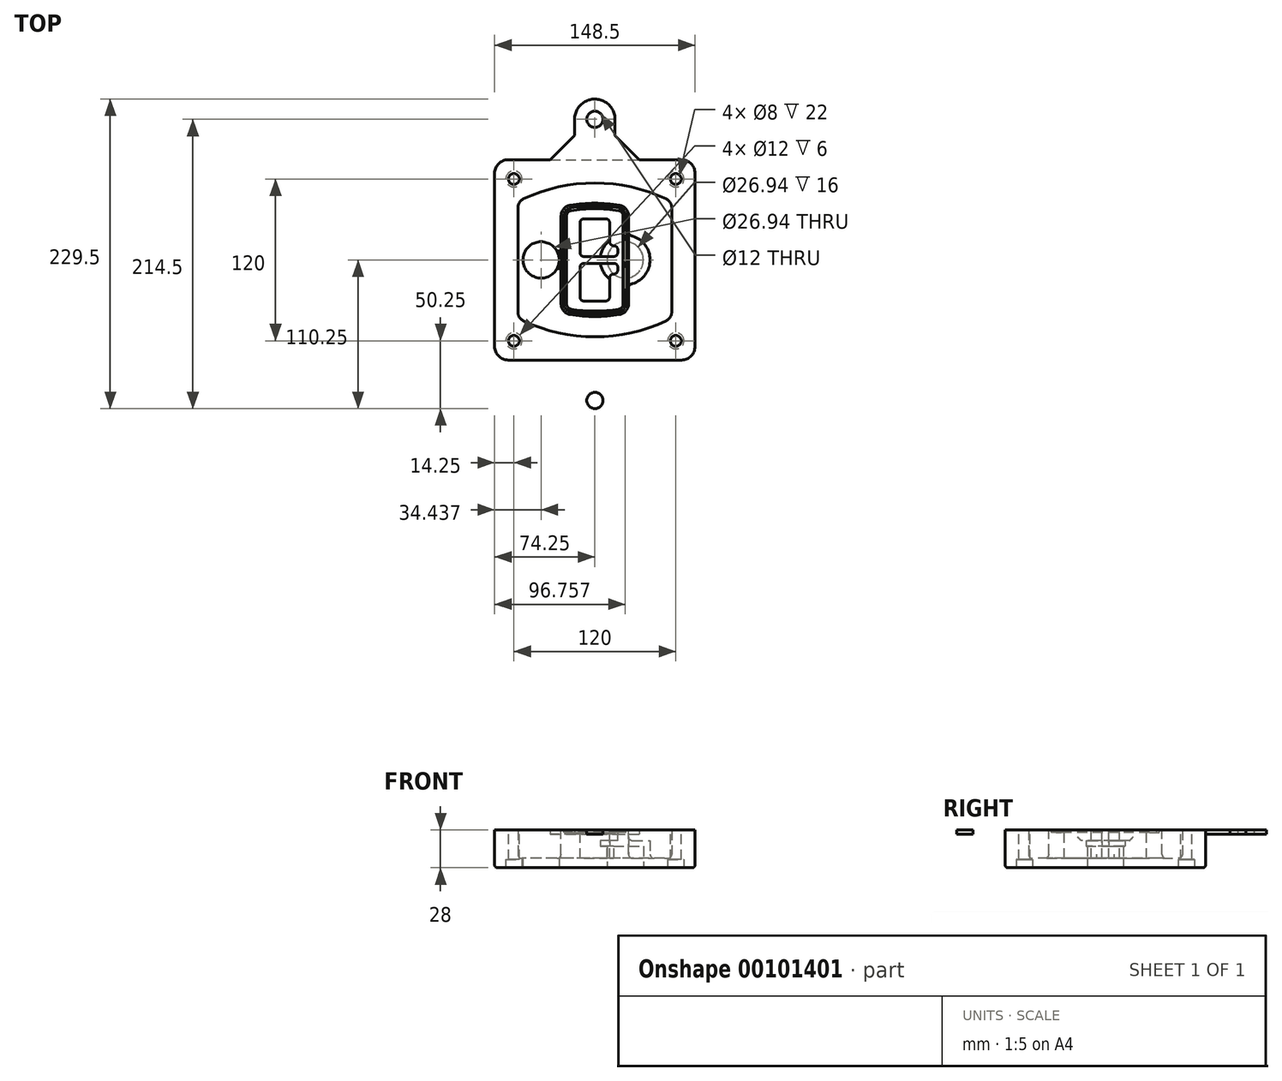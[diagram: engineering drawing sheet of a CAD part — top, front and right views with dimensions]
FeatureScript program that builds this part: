
annotation { "Feature Type Name" : "Feature", "Feature Type Description" : "" }
export const myFeature = defineFeature(function(context is Context, id is Id, definition is map)
    precondition{}
    {
        {
            var Q0;
            Q0=qCreatedBy(makeId("Top.planeOp"),FACE);
            var sketch = newSketch(context, id + "F0", { "sketchPlane" : qUnion([Q0])});
            skPoint(sketch, "E0.rect.middle", {"position": v(0, 0) * mm});
            skLineSegment(sketch, "E1.bottom", {"start": v(-64.25, -74.25) * mm, "end": v(64.25, -74.25) * mm});
            skLineSegment(sketch, "E1.top", {"start": v(-64.25, 74.25) * mm, "end": v(64.25, 74.25) * mm});
            skLineSegment(sketch, "E1.left", {"start": v(-74.25, -64.25) * mm, "end": v(-74.25, 64.25) * mm});
            skLineSegment(sketch, "E1.right", {"start": v(74.25, -64.25) * mm, "end": v(74.25, 64.25) * mm});
            skLineSegment(sketch, "E2", {"start": v(-74.25, 74.25) * mm, "end": v(74.25, -74.25) * mm, "construction": true});
            skLineSegment(sketch, "E3", {"start": v(74.25, 74.25) * mm, "end": v(-74.25, -74.25) * mm, "construction": true});
            skCircle(sketch, "E4", {"center": v(-60, 60) * mm, "radius": 4 * mm});
            skCircle(sketch, "E5", {"center": v(60, 60) * mm, "radius": 4 * mm});
            skCircle(sketch, "E6", {"center": v(60, -60) * mm, "radius": 4 * mm});
            skCircle(sketch, "E7", {"center": v(-60, -60) * mm, "radius": 4 * mm});
            skLineSegment(sketch, "E8", {"start": v(-60, 60) * mm, "end": v(60, 60) * mm, "construction": true});
            skLineSegment(sketch, "E9", {"start": v(60, 60) * mm, "end": v(60, -60) * mm, "construction": true});
            skLineSegment(sketch, "E10", {"start": v(60, -60) * mm, "end": v(-60, -60) * mm, "construction": true});
            skLineSegment(sketch, "E11", {"start": v(-60, -60) * mm, "end": v(-60, 60) * mm, "construction": true});
            skLineSegment(sketch, "E12", {"start": v(-60, 38.83) * mm, "end": v(-60, -38.83) * mm});
            skLineSegment(sketch, "E13", {"start": v(60, 38.83) * mm, "end": v(60, -38.83) * mm});
            skArc(sketch, "E14", {"start": v(54.26, 47.88) * mm, "mid": v(0, 60) * mm, "end": v(-54.26, 47.88) * mm});
            skArc(sketch, "E15", {"start": v(-54.26, -47.88) * mm, "mid": v(0, -60) * mm, "end": v(54.26, -47.88) * mm});
            skLineSegment(sketch, "E16", {"start": v(-60, 0) * mm, "end": v(60, 0) * mm, "construction": true});
            skPoint(sketch, "E17.visualSharp", {"position": v(-60, -45) * mm});
            skArc(sketch, "E17.filletArc", {"start": v(-60, -38.83) * mm, "mid": v(-58.44, -44.2) * mm, "end": v(-54.26, -47.88) * mm});
            skPoint(sketch, "E18.visualSharp", {"position": v(-60, 45) * mm});
            skArc(sketch, "E18.filletArc", {"start": v(-54.26, 47.88) * mm, "mid": v(-58.44, 44.2) * mm, "end": v(-60, 38.83) * mm});
            skPoint(sketch, "E19.visualSharp", {"position": v(60, 45) * mm});
            skArc(sketch, "E19.filletArc", {"start": v(60, 38.83) * mm, "mid": v(58.44, 44.2) * mm, "end": v(54.26, 47.88) * mm});
            skPoint(sketch, "E20.visualSharp", {"position": v(60, -45) * mm});
            skArc(sketch, "E20.filletArc", {"start": v(54.26, -47.88) * mm, "mid": v(58.44, -44.2) * mm, "end": v(60, -38.83) * mm});
            skPoint(sketch, "E21.visualSharp", {"position": v(-74.25, 74.25) * mm});
            skArc(sketch, "E21.filletArc", {"start": v(-64.25, 74.25) * mm, "mid": v(-71.32, 71.32) * mm, "end": v(-74.25, 64.25) * mm});
            skPoint(sketch, "E22.visualSharp", {"position": v(74.25, 74.25) * mm});
            skArc(sketch, "E22.filletArc", {"start": v(74.25, 64.25) * mm, "mid": v(71.32, 71.32) * mm, "end": v(64.25, 74.25) * mm});
            skPoint(sketch, "E23.visualSharp", {"position": v(74.25, -74.25) * mm});
            skArc(sketch, "E23.filletArc", {"start": v(64.25, -74.25) * mm, "mid": v(71.32, -71.32) * mm, "end": v(74.25, -64.25) * mm});
            skPoint(sketch, "E24.visualSharp", {"position": v(-74.25, -74.25) * mm});
            skArc(sketch, "E24.filletArc", {"start": v(-74.25, -64.25) * mm, "mid": v(-71.32, -71.32) * mm, "end": v(-64.25, -74.25) * mm});
            skArc(sketch, "E25.0", {"start": v(57, 38.83) * mm, "mid": v(55.9, 42.58) * mm, "end": v(52.98, 45.17) * mm});
            skLineSegment(sketch, "E25.1", {"start": v(57, 38.83) * mm, "end": v(57, -38.83) * mm});
            skArc(sketch, "E25.2", {"start": v(52.98, -45.17) * mm, "mid": v(55.9, -42.58) * mm, "end": v(57, -38.83) * mm});
            skArc(sketch, "E25.3", {"start": v(-52.98, -45.17) * mm, "mid": v(0, -57) * mm, "end": v(52.98, -45.17) * mm});
            skArc(sketch, "E25.4", {"start": v(-57, -38.83) * mm, "mid": v(-55.9, -42.58) * mm, "end": v(-52.98, -45.17) * mm});
            skArc(sketch, "E25.5", {"start": v(52.98, 45.17) * mm, "mid": v(0, 57) * mm, "end": v(-52.98, 45.17) * mm});
            skLineSegment(sketch, "E25.6", {"start": v(-57, 38.83) * mm, "end": v(-57, -38.83) * mm});
            skArc(sketch, "E25.7", {"start": v(-52.98, 45.17) * mm, "mid": v(-55.9, 42.58) * mm, "end": v(-57, 38.83) * mm});
            skArc(sketch, "E26.0", {"start": v(-55.96, 51.5) * mm, "mid": v(-61.82, 46.33) * mm, "end": v(-64, 38.83) * mm});
            skArc(sketch, "E26.1", {"start": v(55.96, 51.5) * mm, "mid": v(0, 64) * mm, "end": v(-55.96, 51.5) * mm});
            skArc(sketch, "E26.2", {"start": v(64, 38.83) * mm, "mid": v(61.82, 46.33) * mm, "end": v(55.96, 51.5) * mm});
            skLineSegment(sketch, "E26.3", {"start": v(64, 38.83) * mm, "end": v(64, -38.83) * mm});
            skArc(sketch, "E26.4", {"start": v(55.96, -51.5) * mm, "mid": v(61.82, -46.33) * mm, "end": v(64, -38.83) * mm});
            skLineSegment(sketch, "E26.5", {"start": v(-64, 38.83) * mm, "end": v(-64, -38.83) * mm});
            skArc(sketch, "E26.6", {"start": v(-55.96, -51.5) * mm, "mid": v(0, -64) * mm, "end": v(55.96, -51.5) * mm});
            skArc(sketch, "E26.7", {"start": v(-64, -38.83) * mm, "mid": v(-61.82, -46.33) * mm, "end": v(-55.96, -51.5) * mm});
            skSolve(sketch);
        }
        {
            var Q0;
            Q0=makeQuery(id+"F0.imprint","IMPRINT",FACE,{"disambiguationData":[TD([[makeQuery(id+"F0.imprint","IMPRINT",EDGE,{"derivedFrom":sQuery(id+"F0.wireOp",EDGE,"E1.bottom")}),1.0]])]});
            var Q1;
            Q1=makeQuery(id+"F0.imprint","IMPRINT",FACE,{"disambiguationData":[TD([[makeQuery(id+"F0.imprint","IMPRINT",EDGE,{"derivedFrom":sQuery(id+"F0.wireOp",EDGE,"E12")}),1.0]])]});
            var Q2;
            Q2=makeQuery(id+"F0.imprint","IMPRINT",FACE,{"disambiguationData":[TD([[makeQuery(id+"F0.imprint","IMPRINT",EDGE,{"derivedFrom":sQuery(id+"F0.wireOp",EDGE,"E25.0")}),1.0]])]});
            var Q3;
            Q3=makeQuery(id+"F0.imprint","IMPRINT",FACE,{"disambiguationData":[TD([[makeQuery(id+"F0.imprint","IMPRINT",EDGE,{"derivedFrom":sQuery(id+"F0.wireOp",EDGE,"E12")}),-1.0]])]});
            extrude(context, id + "F1", {"entities" : qUnion([Q0, Q1, Q2, Q3]), "oppositeDirection" : true, "depth" : 25 * mm});
        }
        {
            var Q0;
            Q0=makeQuery(id+"F0.imprint","IMPRINT",FACE,{"disambiguationData":[TD([[makeQuery(id+"F0.imprint","IMPRINT",EDGE,{"derivedFrom":sQuery(id+"F0.wireOp",EDGE,"E12")}),1.0]])]});
            extrude(context, id + "F2", {"entities" : qUnion([Q0]), "operationType" : NewBodyOperationType.ADD, "depth" : 3 * mm});
        }
        {
            var Q0;
            Q0=makeQuery(id+"F0.imprint","IMPRINT",FACE,{"disambiguationData":[TD([[makeQuery(id+"F0.imprint","IMPRINT",EDGE,{"derivedFrom":sQuery(id+"F0.wireOp",EDGE,"E25.0")}),1.0]])]});
            extrude(context, id + "F3", {"entities" : qUnion([Q0]), "operationType" : NewBodyOperationType.REMOVE, "oppositeDirection" : true, "depth" : 18 * mm});
        }
        {
            var Q0;
            Q0=makeQuery(id+"F2.opExtrude","CAP_FACE",FACE,{"disambiguationData":[OSD([sQuery(id+"F0.wireOp",EDGE,"E12"),sQuery(id+"F0.wireOp",EDGE,"E13"),sQuery(id+"F0.wireOp",EDGE,"E14"),sQuery(id+"F0.wireOp",EDGE,"E15"),sQuery(id+"F0.wireOp",EDGE,"E17.filletArc"),sQuery(id+"F0.wireOp",EDGE,"E18.filletArc"),sQuery(id+"F0.wireOp",EDGE,"E19.filletArc"),sQuery(id+"F0.wireOp",EDGE,"E20.filletArc"),sQuery(id+"F0.wireOp",EDGE,"E25.0"),sQuery(id+"F0.wireOp",EDGE,"E25.1"),sQuery(id+"F0.wireOp",EDGE,"E25.2"),sQuery(id+"F0.wireOp",EDGE,"E25.3"),sQuery(id+"F0.wireOp",EDGE,"E25.4"),sQuery(id+"F0.wireOp",EDGE,"E25.5"),sQuery(id+"F0.wireOp",EDGE,"E25.6"),sQuery(id+"F0.wireOp",EDGE,"E25.7")])],"isStart":false});
            var sketch = newSketch(context, id + "F4", { "sketchPlane" : qUnion([Q0])});
            skArc(sketch, "E27.0", {"start": v(-18.34, -40.45) * mm, "mid": v(0, -42) * mm, "end": v(18.34, -40.45) * mm});
            skArc(sketch, "E28.0", {"start": v(18.34, 40.45) * mm, "mid": v(0, 42) * mm, "end": v(-18.34, 40.45) * mm});
            skLineSegment(sketch, "E29", {"start": v(-25, 32.57) * mm, "end": v(-25, -32.57) * mm});
            skLineSegment(sketch, "E30", {"start": v(25, 32.57) * mm, "end": v(25, -32.57) * mm});
            skLineSegment(sketch, "E31", {"start": v(-25, 39.1) * mm, "end": v(25, 39.1) * mm, "construction": true});
            skLineSegment(sketch, "E32", {"start": v(-25, -39.1) * mm, "end": v(25, -39.1) * mm, "construction": true});
            skPoint(sketch, "E33.visualSharp", {"position": v(-25, 39.1) * mm});
            skArc(sketch, "E33.filletArc", {"start": v(-18.34, 40.45) * mm, "mid": v(-23.11, 37.73) * mm, "end": v(-25, 32.57) * mm});
            skPoint(sketch, "E34.visualSharp", {"position": v(25, 39.1) * mm});
            skArc(sketch, "E34.filletArc", {"start": v(25, 32.57) * mm, "mid": v(23.11, 37.73) * mm, "end": v(18.34, 40.45) * mm});
            skPoint(sketch, "E35.visualSharp", {"position": v(25, -39.1) * mm});
            skArc(sketch, "E35.filletArc", {"start": v(18.34, -40.45) * mm, "mid": v(23.11, -37.73) * mm, "end": v(25, -32.57) * mm});
            skPoint(sketch, "E36.visualSharp", {"position": v(-25, -39.1) * mm});
            skArc(sketch, "E36.filletArc", {"start": v(-25, -32.57) * mm, "mid": v(-23.11, -37.73) * mm, "end": v(-18.34, -40.45) * mm});
            skArc(sketch, "E37.0", {"start": v(52.98, 45.17) * mm, "mid": v(0, 57) * mm, "end": v(-52.98, 45.17) * mm});
            skArc(sketch, "E37.1", {"start": v(-52.98, 45.17) * mm, "mid": v(-55.9, 42.58) * mm, "end": v(-57, 38.83) * mm});
            skLineSegment(sketch, "E37.2", {"start": v(-57, 38.83) * mm, "end": v(-57, -38.83) * mm});
            skArc(sketch, "E37.3", {"start": v(-57, -38.83) * mm, "mid": v(-55.9, -42.58) * mm, "end": v(-52.98, -45.17) * mm});
            skArc(sketch, "E37.4", {"start": v(-52.98, -45.17) * mm, "mid": v(0, -57) * mm, "end": v(52.98, -45.17) * mm});
            skArc(sketch, "E37.5", {"start": v(52.98, -45.17) * mm, "mid": v(55.9, -42.58) * mm, "end": v(57, -38.83) * mm});
            skLineSegment(sketch, "E37.6", {"start": v(57, 38.83) * mm, "end": v(57, -38.83) * mm});
            skArc(sketch, "E37.7", {"start": v(57, 38.83) * mm, "mid": v(55.9, 42.58) * mm, "end": v(52.98, 45.17) * mm});
            skLineSegment(sketch, "E38.0", {"start": v(23, 32.57) * mm, "end": v(23, -32.57) * mm});
            skArc(sketch, "E38.1", {"start": v(18, -38.48) * mm, "mid": v(21.58, -36.44) * mm, "end": v(23, -32.57) * mm});
            skArc(sketch, "E38.2", {"start": v(-18, -38.48) * mm, "mid": v(0, -40) * mm, "end": v(18, -38.48) * mm});
            skArc(sketch, "E38.3", {"start": v(-23, -32.57) * mm, "mid": v(-21.58, -36.44) * mm, "end": v(-18, -38.48) * mm});
            skLineSegment(sketch, "E38.4", {"start": v(-23, 32.57) * mm, "end": v(-23, -32.57) * mm});
            skArc(sketch, "E38.5", {"start": v(23, 32.57) * mm, "mid": v(21.58, 36.44) * mm, "end": v(18, 38.48) * mm});
            skArc(sketch, "E38.6", {"start": v(-18, 38.48) * mm, "mid": v(-21.58, 36.44) * mm, "end": v(-23, 32.57) * mm});
            skArc(sketch, "E38.7", {"start": v(18, 38.48) * mm, "mid": v(0, 40) * mm, "end": v(-18, 38.48) * mm});
            skArc(sketch, "E39.0", {"start": v(21, 32.57) * mm, "mid": v(20.06, 35.15) * mm, "end": v(17.67, 36.5) * mm});
            skLineSegment(sketch, "E39.1", {"start": v(21, 32.57) * mm, "end": v(21, -32.57) * mm});
            skArc(sketch, "E39.2", {"start": v(17.67, -36.5) * mm, "mid": v(20.06, -35.15) * mm, "end": v(21, -32.57) * mm});
            skArc(sketch, "E39.3", {"start": v(-17.67, -36.5) * mm, "mid": v(0, -38) * mm, "end": v(17.67, -36.5) * mm});
            skArc(sketch, "E39.4", {"start": v(-21, -32.57) * mm, "mid": v(-20.06, -35.15) * mm, "end": v(-17.67, -36.5) * mm});
            skArc(sketch, "E39.5", {"start": v(17.67, 36.5) * mm, "mid": v(0, 38) * mm, "end": v(-17.67, 36.5) * mm});
            skLineSegment(sketch, "E39.6", {"start": v(-21, 32.57) * mm, "end": v(-21, -32.57) * mm});
            skArc(sketch, "E39.7", {"start": v(-17.67, 36.5) * mm, "mid": v(-20.06, 35.15) * mm, "end": v(-21, 32.57) * mm});
            skLineSegment(sketch, "E40", {"start": v(-25, 0) * mm, "end": v(25, 0) * mm, "construction": true});
            skLineSegment(sketch, "E41", {"start": v(-11, 5.5) * mm, "end": v(-11, 27.5) * mm});
            skLineSegment(sketch, "E42", {"start": v(-8, 30.5) * mm, "end": v(8, 30.5) * mm});
            skLineSegment(sketch, "E43", {"start": v(11, 27.5) * mm, "end": v(11, 13.5) * mm});
            skLineSegment(sketch, "E44", {"start": v(14, 10.5) * mm, "end": v(14, 10.5) * mm});
            skLineSegment(sketch, "E45", {"start": v(17, 7.5) * mm, "end": v(17, 5.5) * mm});
            skLineSegment(sketch, "E46", {"start": v(14, 2.5) * mm, "end": v(-8, 2.5) * mm});
            skPoint(sketch, "E47.visualSharp", {"position": v(-11, 30.5) * mm});
            skArc(sketch, "E47.filletArc", {"start": v(-8, 30.5) * mm, "mid": v(-10.12, 29.62) * mm, "end": v(-11, 27.5) * mm});
            skPoint(sketch, "E48.visualSharp", {"position": v(11, 30.5) * mm});
            skArc(sketch, "E48.filletArc", {"start": v(11, 27.5) * mm, "mid": v(10.12, 29.62) * mm, "end": v(8, 30.5) * mm});
            skPoint(sketch, "E49.visualSharp", {"position": v(11, 10.5) * mm});
            skArc(sketch, "E49.filletArc", {"start": v(11, 13.5) * mm, "mid": v(11.88, 11.38) * mm, "end": v(14, 10.5) * mm});
            skPoint(sketch, "E50.visualSharp", {"position": v(17, 10.5) * mm});
            skArc(sketch, "E50.filletArc", {"start": v(17, 7.5) * mm, "mid": v(16.12, 9.62) * mm, "end": v(14, 10.5) * mm});
            skPoint(sketch, "E51.visualSharp", {"position": v(17, 2.5) * mm});
            skArc(sketch, "E51.filletArc", {"start": v(14, 2.5) * mm, "mid": v(16.12, 3.38) * mm, "end": v(17, 5.5) * mm});
            skPoint(sketch, "E52.visualSharp", {"position": v(-11, 2.5) * mm});
            skArc(sketch, "E52.filletArc", {"start": v(-11, 5.5) * mm, "mid": v(-10.12, 3.38) * mm, "end": v(-8, 2.5) * mm});
            skLineSegment(sketch, "E53.0.MirrorCS", {"start": v(14, -2.5) * mm, "end": v(-8, -2.5) * mm});
            skArc(sketch, "E54.0.MirrorCS", {"start": v(-11, -5.5) * mm, "mid": v(-10.12, -3.38) * mm, "end": v(-8, -2.5) * mm});
            skLineSegment(sketch, "E55.0.MirrorCS", {"start": v(-11, -5.5) * mm, "end": v(-11, -27.5) * mm});
            skArc(sketch, "E56.0.MirrorCS", {"start": v(-8, -30.5) * mm, "mid": v(-10.12, -29.62) * mm, "end": v(-11, -27.5) * mm});
            skLineSegment(sketch, "E57.0.MirrorCS", {"start": v(-8, -30.5) * mm, "end": v(8, -30.5) * mm});
            skArc(sketch, "E58.0.MirrorCS", {"start": v(11, -27.5) * mm, "mid": v(10.12, -29.62) * mm, "end": v(8, -30.5) * mm});
            skLineSegment(sketch, "E59.0.MirrorCS", {"start": v(11, -27.5) * mm, "end": v(11, -13.5) * mm});
            skArc(sketch, "E60.0.MirrorCS", {"start": v(11, -13.5) * mm, "mid": v(11.88, -11.38) * mm, "end": v(14, -10.5) * mm});
            skArc(sketch, "E61.0.MirrorCS", {"start": v(17, -7.5) * mm, "mid": v(16.12, -9.62) * mm, "end": v(14, -10.5) * mm});
            skLineSegment(sketch, "E62.0.MirrorCS", {"start": v(17, -7.5) * mm, "end": v(17, -5.5) * mm});
            skArc(sketch, "E63.0.MirrorCS", {"start": v(14, -2.5) * mm, "mid": v(16.12, -3.38) * mm, "end": v(17, -5.5) * mm});
            skSolve(sketch);
        }
        {
            var Q0;
            Q0=makeQuery(id+"F4.imprint","IMPRINT",FACE,{"disambiguationData":[TD([[makeQuery(id+"F4.imprint","IMPRINT",EDGE,{"derivedFrom":sQuery(id+"F4.wireOp",EDGE,"E27.0")}),1.0]])]});
            var Q1;
            Q1=makeQuery(id+"F4.imprint","IMPRINT",FACE,{"disambiguationData":[TD([[makeQuery(id+"F4.imprint","IMPRINT",EDGE,{"derivedFrom":sQuery(id+"F4.wireOp",EDGE,"E38.0")}),-1.0]])]});
            var Q2;
            Q2=makeQuery(id+"F4.imprint","IMPRINT",FACE,{"disambiguationData":[TD([[makeQuery(id+"F4.imprint","IMPRINT",EDGE,{"derivedFrom":sQuery(id+"F4.wireOp",EDGE,"E39.0")}),1.0]])]});
            extrude(context, id + "F5", {"entities" : qUnion([Q0, Q1, Q2]), "operationType" : NewBodyOperationType.ADD, "endBound" : BoundingType.UP_TO_NEXT, "oppositeDirection" : true, "depth" : 25 * mm});
        }
        {
            var Q0;
            Q0=makeQuery(id+"F4.imprint","IMPRINT",FACE,{"disambiguationData":[TD([[makeQuery(id+"F4.imprint","IMPRINT",EDGE,{"derivedFrom":sQuery(id+"F4.wireOp",EDGE,"E38.0")}),-1.0]])]});
            extrude(context, id + "F6", {"entities" : qUnion([Q0]), "operationType" : NewBodyOperationType.REMOVE, "oppositeDirection" : true, "depth" : 2 * mm});
        }
        {
            var Q0;
            Q0=makeQuery(id+"F1.opExtrude","CAP_FACE",FACE,{"disambiguationData":[OSD([sQuery(id+"F0.wireOp",EDGE,"E1.bottom"),sQuery(id+"F0.wireOp",EDGE,"E1.top"),sQuery(id+"F0.wireOp",EDGE,"E1.left"),sQuery(id+"F0.wireOp",EDGE,"E1.right"),sQuery(id+"F0.wireOp",EDGE,"E4"),sQuery(id+"F0.wireOp",EDGE,"E5"),sQuery(id+"F0.wireOp",EDGE,"E6"),sQuery(id+"F0.wireOp",EDGE,"E7"),sQuery(id+"F0.wireOp",EDGE,"E21.filletArc"),sQuery(id+"F0.wireOp",EDGE,"E22.filletArc"),sQuery(id+"F0.wireOp",EDGE,"E23.filletArc"),sQuery(id+"F0.wireOp",EDGE,"E24.filletArc")])],"isStart":false});
            var sketch = newSketch(context, id + "F7", { "sketchPlane" : qUnion([Q0])});
            skCircle(sketch, "E64", {"center": v(22.5, 0) * mm, "radius": 13.47 * mm});
            skCircle(sketch, "E65", {"center": v(-39.81, 0) * mm, "radius": 13.47 * mm});
            skLineSegment(sketch, "E66", {"start": v(74.25, 0) * mm, "end": v(-74.25, 0) * mm});
            skCircle(sketch, "E67", {"center": v(22.5, 0) * mm, "radius": 18.47 * mm});
            skCircle(sketch, "E68", {"center": v(60, -60) * mm, "radius": 6 * mm});
            skCircle(sketch, "E69", {"center": v(-60, -60) * mm, "radius": 6 * mm});
            skCircle(sketch, "E70", {"center": v(-60, 60) * mm, "radius": 6 * mm});
            skCircle(sketch, "E71", {"center": v(60, 60) * mm, "radius": 6 * mm});
            skSolve(sketch);
        }
        {
            var Q0;
            {var subQ1=sQuery(id+"F7.wireOp",EDGE,"E66");var subQ4=sQuery(id+"F7.wireOp",EDGE,"E64");var subQ6=makeQuery(id+"F7.imprint","INTERSECT",VERTEX,{"disambiguationData":[OD(0.0)],"derivedFrom":[subQ4,subQ1]});Q0=makeQuery(id+"F7.imprint","IMPRINT",FACE,{"disambiguationData":[TD([[makeQuery(id+"F7.imprint","IMPRINT",EDGE,{"disambiguationData":[TD([[subQ6,-1.0]])],"derivedFrom":subQ4}),-1.0]])]});}
            var Q1;
            {var subQ0=sQuery(id+"F7.wireOp",EDGE,"E66");var subQ1=sQuery(id+"F7.wireOp",EDGE,"E64");var subQ3=makeQuery(id+"F7.imprint","INTERSECT",VERTEX,{"disambiguationData":[OD(0.0)],"derivedFrom":[subQ1,subQ0]});Q1=makeQuery(id+"F7.imprint","IMPRINT",FACE,{"disambiguationData":[TD([[makeQuery(id+"F7.imprint","IMPRINT",EDGE,{"disambiguationData":[TD([[subQ3,-1.0]])],"derivedFrom":subQ1}),1.0]])]});}
            var Q2;
            {var subQ0=sQuery(id+"F7.wireOp",EDGE,"E66");var subQ1=sQuery(id+"F7.wireOp",EDGE,"E64");var subQ3=makeQuery(id+"F7.imprint","INTERSECT",VERTEX,{"disambiguationData":[OD(0.0)],"derivedFrom":[subQ1,subQ0]});Q2=makeQuery(id+"F7.imprint","IMPRINT",FACE,{"disambiguationData":[TD([[makeQuery(id+"F7.imprint","IMPRINT",EDGE,{"disambiguationData":[TD([[subQ3,1.0]])],"derivedFrom":subQ1}),1.0]])]});}
            var Q3;
            {var subQ1=sQuery(id+"F7.wireOp",EDGE,"E66");var subQ4=sQuery(id+"F7.wireOp",EDGE,"E64");var subQ6=makeQuery(id+"F7.imprint","INTERSECT",VERTEX,{"disambiguationData":[OD(0.0)],"derivedFrom":[subQ4,subQ1]});Q3=makeQuery(id+"F7.imprint","IMPRINT",FACE,{"disambiguationData":[TD([[makeQuery(id+"F7.imprint","IMPRINT",EDGE,{"disambiguationData":[TD([[subQ6,1.0]])],"derivedFrom":subQ4}),-1.0]])]});}
            extrude(context, id + "F8", {"entities" : qUnion([Q0, Q1, Q2, Q3]), "operationType" : NewBodyOperationType.ADD, "oppositeDirection" : true, "depth" : 20 * mm});
        }
        {
            var Q0;
            {var subQ0=sQuery(id+"F7.wireOp",EDGE,"E66");var subQ1=sQuery(id+"F7.wireOp",EDGE,"E64");var subQ3=makeQuery(id+"F7.imprint","INTERSECT",VERTEX,{"disambiguationData":[OD(0.0)],"derivedFrom":[subQ1,subQ0]});Q0=makeQuery(id+"F7.imprint","IMPRINT",FACE,{"disambiguationData":[TD([[makeQuery(id+"F7.imprint","IMPRINT",EDGE,{"disambiguationData":[TD([[subQ3,-1.0]])],"derivedFrom":subQ1}),1.0]])]});}
            var Q1;
            {var subQ0=sQuery(id+"F7.wireOp",EDGE,"E66");var subQ1=sQuery(id+"F7.wireOp",EDGE,"E64");var subQ3=makeQuery(id+"F7.imprint","INTERSECT",VERTEX,{"disambiguationData":[OD(0.0)],"derivedFrom":[subQ1,subQ0]});Q1=makeQuery(id+"F7.imprint","IMPRINT",FACE,{"disambiguationData":[TD([[makeQuery(id+"F7.imprint","IMPRINT",EDGE,{"disambiguationData":[TD([[subQ3,1.0]])],"derivedFrom":subQ1}),1.0]])]});}
            extrude(context, id + "F9", {"entities" : qUnion([Q0, Q1]), "operationType" : NewBodyOperationType.REMOVE, "oppositeDirection" : true, "depth" : 16 * mm});
        }
        {
            var Q0;
            {var subQ0=sQuery(id+"F7.wireOp",EDGE,"E66");var subQ1=sQuery(id+"F7.wireOp",EDGE,"E65");var subQ3=makeQuery(id+"F7.imprint","INTERSECT",VERTEX,{"disambiguationData":[OD(0.0)],"derivedFrom":[subQ1,subQ0]});Q0=makeQuery(id+"F7.imprint","IMPRINT",FACE,{"disambiguationData":[TD([[makeQuery(id+"F7.imprint","IMPRINT",EDGE,{"disambiguationData":[TD([[subQ3,-1.0]])],"derivedFrom":subQ1}),1.0]])]});}
            var Q1;
            {var subQ0=sQuery(id+"F7.wireOp",EDGE,"E66");var subQ1=sQuery(id+"F7.wireOp",EDGE,"E65");var subQ3=makeQuery(id+"F7.imprint","INTERSECT",VERTEX,{"disambiguationData":[OD(0.0)],"derivedFrom":[subQ1,subQ0]});Q1=makeQuery(id+"F7.imprint","IMPRINT",FACE,{"disambiguationData":[TD([[makeQuery(id+"F7.imprint","IMPRINT",EDGE,{"disambiguationData":[TD([[subQ3,1.0]])],"derivedFrom":subQ1}),1.0]])]});}
            extrude(context, id + "F10", {"entities" : qUnion([Q0, Q1]), "operationType" : NewBodyOperationType.REMOVE, "oppositeDirection" : true, "depth" : 25 * mm});
        }
        {
            var Q0;
            Q0=makeQuery(id+"F7.imprint","IMPRINT",FACE,{"disambiguationData":[TD([[makeQuery(id+"F7.imprint","IMPRINT",EDGE,{"derivedFrom":sQuery(id+"F7.wireOp",EDGE,"E68")}),1.0]])]});
            var Q1;
            Q1=makeQuery(id+"F7.imprint","IMPRINT",FACE,{"disambiguationData":[TD([[makeQuery(id+"F7.imprint","IMPRINT",EDGE,{"derivedFrom":makeQuery(id+"F1.opExtrude","CAP_EDGE",EDGE,{"disambiguationData":[OSD([sQuery(id+"F0.wireOp",EDGE,"E5")])],"isStart":false})}),-1.0]])]});
            var Q2;
            Q2=makeQuery(id+"F7.imprint","IMPRINT",FACE,{"disambiguationData":[TD([[makeQuery(id+"F7.imprint","IMPRINT",EDGE,{"derivedFrom":sQuery(id+"F7.wireOp",EDGE,"E69")}),1.0]])]});
            var Q3;
            Q3=makeQuery(id+"F7.imprint","IMPRINT",FACE,{"disambiguationData":[TD([[makeQuery(id+"F7.imprint","IMPRINT",EDGE,{"derivedFrom":makeQuery(id+"F1.opExtrude","CAP_EDGE",EDGE,{"disambiguationData":[OSD([sQuery(id+"F0.wireOp",EDGE,"E4")])],"isStart":false})}),-1.0]])]});
            var Q4;
            Q4=makeQuery(id+"F7.imprint","IMPRINT",FACE,{"disambiguationData":[TD([[makeQuery(id+"F7.imprint","IMPRINT",EDGE,{"derivedFrom":sQuery(id+"F7.wireOp",EDGE,"E70")}),1.0]])]});
            var Q5;
            Q5=makeQuery(id+"F7.imprint","IMPRINT",FACE,{"disambiguationData":[TD([[makeQuery(id+"F7.imprint","IMPRINT",EDGE,{"derivedFrom":makeQuery(id+"F1.opExtrude","CAP_EDGE",EDGE,{"disambiguationData":[OSD([sQuery(id+"F0.wireOp",EDGE,"E7")])],"isStart":false})}),-1.0]])]});
            var Q6;
            Q6=makeQuery(id+"F7.imprint","IMPRINT",FACE,{"disambiguationData":[TD([[makeQuery(id+"F7.imprint","IMPRINT",EDGE,{"derivedFrom":sQuery(id+"F7.wireOp",EDGE,"E71")}),1.0]])]});
            var Q7;
            Q7=makeQuery(id+"F7.imprint","IMPRINT",FACE,{"disambiguationData":[TD([[makeQuery(id+"F7.imprint","IMPRINT",EDGE,{"derivedFrom":makeQuery(id+"F1.opExtrude","CAP_EDGE",EDGE,{"disambiguationData":[OSD([sQuery(id+"F0.wireOp",EDGE,"E6")])],"isStart":false})}),-1.0]])]});
            extrude(context, id + "F11", {"entities" : qUnion([Q0, Q1, Q2, Q3, Q4, Q5, Q6, Q7]), "operationType" : NewBodyOperationType.REMOVE, "oppositeDirection" : true, "depth" : 6 * mm});
        }
        {
            var Q0;
            Q0=makeQuery(id+"F9.boolean.opBoolean","COPY",FACE,{"derivedFrom":makeQuery(id+"F9.opExtrude","CAP_FACE",FACE,{"disambiguationData":[OSD([sQuery(id+"F7.wireOp",EDGE,"E64")])],"isStart":false})});
            var sketch = newSketch(context, id + "F12", { "sketchPlane" : qUnion([Q0])});
            skArc(sketch, "E72.0", {"start": v(11, 14.45) * mm, "mid": v(6.45, 9.13) * mm, "end": v(4.2, 2.5) * mm});
            skArc(sketch, "E72.1", {"start": v(4.2, -2.5) * mm, "mid": v(6.45, -9.13) * mm, "end": v(11, -14.45) * mm});
            skLineSegment(sketch, "E73", {"start": v(4.2, -2.5) * mm, "end": v(14, -2.5) * mm});
            skLineSegment(sketch, "E74.0", {"start": v(14, 2.5) * mm, "end": v(4.2, 2.5) * mm});
            skArc(sketch, "E74.1", {"start": v(14, 2.5) * mm, "mid": v(16.12, 3.38) * mm, "end": v(17, 5.5) * mm});
            skLineSegment(sketch, "E74.2", {"start": v(17, 7.5) * mm, "end": v(17, 5.5) * mm});
            skArc(sketch, "E74.3", {"start": v(17, 7.5) * mm, "mid": v(16.12, 9.62) * mm, "end": v(14, 10.5) * mm});
            skArc(sketch, "E74.4", {"start": v(11, 13.5) * mm, "mid": v(11.88, 11.38) * mm, "end": v(14, 10.5) * mm});
            skLineSegment(sketch, "E74.5", {"start": v(11, 14.45) * mm, "end": v(11, 13.5) * mm});
            skLineSegment(sketch, "E74.7", {"start": v(14, -2.5) * mm, "end": v(4.2, -2.5) * mm});
            skArc(sketch, "E74.8", {"start": v(14, -2.5) * mm, "mid": v(16.12, -3.38) * mm, "end": v(17, -5.5) * mm});
            skLineSegment(sketch, "E74.9", {"start": v(17, -7.5) * mm, "end": v(17, -5.5) * mm});
            skArc(sketch, "E74.10", {"start": v(17, -7.5) * mm, "mid": v(16.12, -9.62) * mm, "end": v(14, -10.5) * mm});
            skArc(sketch, "E74.11", {"start": v(11, -13.5) * mm, "mid": v(11.88, -11.38) * mm, "end": v(14, -10.5) * mm});
            skLineSegment(sketch, "E74.12", {"start": v(11, -14.45) * mm, "end": v(11, -13.5) * mm});
            skPoint(sketch, "E75.orphan", {"position": v(11, -27.5) * mm});
            skPoint(sketch, "E76.orphan", {"position": v(-8, -2.5) * mm});
            skPoint(sketch, "E77.orphan", {"position": v(-8, 2.5) * mm});
            skPoint(sketch, "E78.orphan", {"position": v(11, 27.5) * mm});
            skSolve(sketch);
        }
        {
            var Q0;
            {var subQ7=sQuery(id+"F12.wireOp",EDGE,"E72.0");var subQ14=sQuery(id+"F12.wireOp",EDGE,"E72.1");var subQ16=sQuery(id+"F12.wireOp",EDGE,"E74.1");var subQ18=sQuery(id+"F12.wireOp",EDGE,"E74.8");Q0=qUnion([makeQuery(id+"F12.imprint","IMPRINT",FACE,{"disambiguationData":[TD([[makeQuery(id+"F12.imprint","IMPRINT",EDGE,{"derivedFrom":subQ7}),1.0]])]}),makeQuery(id+"F12.imprint","IMPRINT",FACE,{"disambiguationData":[TD([[makeQuery(id+"F12.imprint","IMPRINT",EDGE,{"derivedFrom":subQ14}),1.0]])]}),makeQuery(id+"F12.imprint","IMPRINT",FACE,{"disambiguationData":[TD([[makeQuery(id+"F12.imprint","IMPRINT",EDGE,{"derivedFrom":subQ16}),1.0]])]}),makeQuery(id+"F12.imprint","IMPRINT",FACE,{"disambiguationData":[TD([[makeQuery(id+"F12.imprint","IMPRINT",EDGE,{"derivedFrom":subQ18}),-1.0]])]})]);}
            var Q1;
            Q1=makeQuery(id+"F5.boolean.opBoolean","SPLIT",FACE,{"disambiguationData":[TD([makeQuery(id+"F5.opExtrude","SWEPT_FACE",FACE,{"disambiguationData":[OSD([sQuery(id+"F4.wireOp",EDGE,"E41")])]})])],"derivedFrom":makeQuery(id+"F3.boolean.opBoolean","COPY",FACE,{"derivedFrom":makeQuery(id+"F3.opExtrude","CAP_FACE",FACE,{"disambiguationData":[OSD([sQuery(id+"F0.wireOp",EDGE,"E25.0"),sQuery(id+"F0.wireOp",EDGE,"E25.1"),sQuery(id+"F0.wireOp",EDGE,"E25.2"),sQuery(id+"F0.wireOp",EDGE,"E25.3"),sQuery(id+"F0.wireOp",EDGE,"E25.4"),sQuery(id+"F0.wireOp",EDGE,"E25.5"),sQuery(id+"F0.wireOp",EDGE,"E25.6"),sQuery(id+"F0.wireOp",EDGE,"E25.7")])],"isStart":false})})});
            extrude(context, id + "F13", {"entities" : qUnion([Q0]), "operationType" : NewBodyOperationType.REMOVE, "endBound" : BoundingType.UP_TO_SURFACE, "endBoundEntityFace" : qUnion([Q1]), "depth" : 25 * mm});
        }
        {
            var Q0;
            Q0=makeQuery(id+"F3.boolean.opBoolean","COPY",EDGE,{"derivedFrom":makeQuery(id+"F3.opExtrude","CAP_EDGE",EDGE,{"disambiguationData":[OSD([sQuery(id+"F0.wireOp",EDGE,"E25.6")])],"isStart":false})});
            var Q1;
            Q1=makeQuery(id+"F8.boolean.opBoolean","INTERSECT",EDGE,{"derivedFrom":[makeQuery(id+"F5.opExtrude","SWEPT_FACE",FACE,{"disambiguationData":[OSD([sQuery(id+"F4.wireOp",EDGE,"E30")])]}),makeQuery(id+"F8.opExtrude","CAP_FACE",FACE,{"disambiguationData":[OSD([sQuery(id+"F7.wireOp",EDGE,"E67")])],"isStart":false})]});
            var Q2;
            Q2=makeQuery(id+"F8.boolean.opBoolean","INTERSECT",EDGE,{"disambiguationData":[OD(1.0)],"derivedFrom":[makeQuery(id+"F5.opExtrude","SWEPT_FACE",FACE,{"disambiguationData":[OSD([sQuery(id+"F4.wireOp",EDGE,"E30")])]}),makeQuery(id+"F8.opExtrude","SWEPT_FACE",FACE,{"disambiguationData":[OSD([sQuery(id+"F7.wireOp",EDGE,"E67")])]})]});
            var Q3;
            {var subQ0=sQuery(id+"F4.wireOp",EDGE,"E30");Q3=makeQuery(id+"F8.boolean.opBoolean","SPLIT",EDGE,{"disambiguationData":[TD([makeQuery(id+"F5.opExtrude","SWEPT_FACE",FACE,{"disambiguationData":[OSD([sQuery(id+"F4.wireOp",EDGE,"E35.filletArc")])]})])],"derivedFrom":makeQuery(id+"F5.opExtrude","CAP_EDGE",EDGE,{"disambiguationData":[OSD([subQ0])],"isStart":false})});}
            var Q4;
            {var subQ0=sQuery(id+"F0.wireOp",EDGE,"E25.7");var subQ1=sQuery(id+"F0.wireOp",EDGE,"E25.1");var subQ2=sQuery(id+"F0.wireOp",EDGE,"E25.6");var subQ3=sQuery(id+"F0.wireOp",EDGE,"E25.5");var subQ4=sQuery(id+"F0.wireOp",EDGE,"E25.4");var subQ5=sQuery(id+"F0.wireOp",EDGE,"E25.0");var subQ6=sQuery(id+"F0.wireOp",EDGE,"E25.2");var subQ7=sQuery(id+"F0.wireOp",EDGE,"E25.3");Q4=makeQuery(id+"F8.boolean.opBoolean","INTERSECT",EDGE,{"derivedFrom":[makeQuery(id+"F5.boolean.opBoolean","SPLIT",FACE,{"disambiguationData":[TD([makeQuery(id+"F2.opExtrude","SWEPT_FACE",FACE,{"disambiguationData":[OSD([subQ5])]})])],"derivedFrom":makeQuery(id+"F3.boolean.opBoolean","COPY",FACE,{"derivedFrom":makeQuery(id+"F3.opExtrude","CAP_FACE",FACE,{"disambiguationData":[OSD([subQ5,subQ1,subQ6,subQ7,subQ4,subQ3,subQ2,subQ0])],"isStart":false})})}),makeQuery(id+"F8.opExtrude","SWEPT_FACE",FACE,{"disambiguationData":[OSD([sQuery(id+"F7.wireOp",EDGE,"E67")])]})]});}
            var Q5;
            Q5=makeQuery(id+"F8.boolean.opBoolean","INTERSECT",EDGE,{"disambiguationData":[OD(0.0)],"derivedFrom":[makeQuery(id+"F5.opExtrude","SWEPT_FACE",FACE,{"disambiguationData":[OSD([sQuery(id+"F4.wireOp",EDGE,"E30")])]}),makeQuery(id+"F8.opExtrude","SWEPT_FACE",FACE,{"disambiguationData":[OSD([sQuery(id+"F7.wireOp",EDGE,"E67")])]})]});
            fillet(context, id + "F14", {"entities" : qUnion([Q0, Q1, Q2, Q3, Q4, Q5]), "radius" : 3 * mm, "tangentPropagation" : true, "allowEdgeOverflow" : false});
        }
        {
            var Q0;
            Q0=makeQuery(id+"F1.opExtrude","CAP_EDGE",EDGE,{"disambiguationData":[OSD([sQuery(id+"F0.wireOp",EDGE,"E1.bottom")])],"isStart":false});
            fillet(context, id + "F15", {"entities" : qUnion([Q0]), "radius" : 2 * mm, "tangentPropagation" : true, "allowEdgeOverflow" : false});
        }
        {
            var Q0;
            {var subQ0=sQuery(id+"F0.wireOp",EDGE,"E22.filletArc");var subQ1=sQuery(id+"F0.wireOp",EDGE,"E7");var subQ2=sQuery(id+"F0.wireOp",EDGE,"E6");var subQ3=sQuery(id+"F0.wireOp",EDGE,"E5");var subQ4=sQuery(id+"F0.wireOp",EDGE,"E4");var subQ5=sQuery(id+"F0.wireOp",EDGE,"E1.bottom");var subQ6=sQuery(id+"F0.wireOp",EDGE,"E21.filletArc");var subQ7=sQuery(id+"F0.wireOp",EDGE,"E1.top");var subQ8=sQuery(id+"F0.wireOp",EDGE,"E1.left");var subQ9=sQuery(id+"F0.wireOp",EDGE,"E1.right");var subQ10=sQuery(id+"F0.wireOp",EDGE,"E23.filletArc");var subQ11=sQuery(id+"F0.wireOp",EDGE,"E24.filletArc");Q0=makeQuery(id+"F2.boolean.opBoolean","SPLIT",FACE,{"disambiguationData":[TD([makeQuery(id+"F1.opExtrude","SWEPT_FACE",FACE,{"disambiguationData":[OSD([subQ5])]})])],"derivedFrom":makeQuery(id+"F1.opExtrude","CAP_FACE",FACE,{"disambiguationData":[OSD([subQ5,subQ7,subQ8,subQ9,subQ4,subQ3,subQ2,subQ1,subQ6,subQ0,subQ10,subQ11])],"isStart":true})});}
            var sketch = newSketch(context, id + "F16", { "sketchPlane" : qUnion([Q0])});
            skLineSegment(sketch, "E79", {"start": v(0, 74.25) * mm, "end": v(0, 104.25) * mm, "construction": true});
            skCircle(sketch, "E80", {"center": v(0, 104.25) * mm, "radius": 6 * mm});
            skLineSegment(sketch, "E81", {"start": v(-15, 92.25) * mm, "end": v(-33, 74.25) * mm});
            skLineSegment(sketch, "E82", {"start": v(-15, 92.25) * mm, "end": v(-15, 104.25) * mm});
            skArc(sketch, "E83", {"start": v(15, 104) * mm, "mid": v(0.12, 119.25) * mm, "end": v(-15, 104.25) * mm});
            skLineSegment(sketch, "E84", {"start": v(15, 104) * mm, "end": v(15, 92.25) * mm});
            skLineSegment(sketch, "E85", {"start": v(15, 92.25) * mm, "end": v(33, 74.25) * mm});
            skLineSegment(sketch, "E86", {"start": v(-74.25, 0) * mm, "end": v(74.25, 0) * mm, "construction": true});
            skCircle(sketch, "E87.MirrorC", {"center": v(0, -104.25) * mm, "radius": 6 * mm});
            skLineSegment(sketch, "E88.MirrorCS", {"start": v(-15, -92.25) * mm, "end": v(-33, -74.25) * mm});
            skLineSegment(sketch, "E89.MirrorCS", {"start": v(15, -104) * mm, "end": v(15, -92.25) * mm});
            skLineSegment(sketch, "E90.MirrorCS", {"start": v(-15, -92.25) * mm, "end": v(-15, -104.25) * mm});
            skArc(sketch, "E91.MirrorCS", {"start": v(15, -104) * mm, "mid": v(0.12, -119.25) * mm, "end": v(-15, -104.25) * mm});
            skLineSegment(sketch, "E92.MirrorCS", {"start": v(15, -92.25) * mm, "end": v(33, -74.25) * mm});
            skLineSegment(sketch, "E93.MirrorCS", {"start": v(0, -74.25) * mm, "end": v(0, -104.25) * mm, "construction": true});
            skSolve(sketch);
        }
        {
            var Q0;
            Q0=makeQuery(id+"F16.imprint","IMPRINT",FACE,{"disambiguationData":[TD([[makeQuery(id+"F16.imprint","IMPRINT",EDGE,{"derivedFrom":sQuery(id+"F16.wireOp",EDGE,"E87.MirrorC")}),1.0]])]});
            var Q1;
            Q1=makeQuery(id+"F16.imprint","IMPRINT",FACE,{"disambiguationData":[TD([[makeQuery(id+"F16.imprint","IMPRINT",EDGE,{"derivedFrom":sQuery(id+"F16.wireOp",EDGE,"E80")}),-1.0]])]});
            var Q2;
            Q2=makeQuery(id+"F16.imprint","IMPRINT",FACE,{"disambiguationData":[TD([[makeQuery(id+"F16.imprint","IMPRINT",EDGE,{"derivedFrom":makeQuery(id+"F1.opExtrude","CAP_EDGE",EDGE,{"disambiguationData":[OSD([sQuery(id+"F0.wireOp",EDGE,"E1.left")])],"isStart":true})}),-1.0]])]});
            var Q3;
            Q3=makeQuery(id+"F2.opExtrude","CAP_FACE",FACE,{"disambiguationData":[OSD([sQuery(id+"F0.wireOp",EDGE,"E12"),sQuery(id+"F0.wireOp",EDGE,"E13"),sQuery(id+"F0.wireOp",EDGE,"E14"),sQuery(id+"F0.wireOp",EDGE,"E15"),sQuery(id+"F0.wireOp",EDGE,"E17.filletArc"),sQuery(id+"F0.wireOp",EDGE,"E18.filletArc"),sQuery(id+"F0.wireOp",EDGE,"E19.filletArc"),sQuery(id+"F0.wireOp",EDGE,"E20.filletArc"),sQuery(id+"F0.wireOp",EDGE,"E25.0"),sQuery(id+"F0.wireOp",EDGE,"E25.1"),sQuery(id+"F0.wireOp",EDGE,"E25.2"),sQuery(id+"F0.wireOp",EDGE,"E25.3"),sQuery(id+"F0.wireOp",EDGE,"E25.4"),sQuery(id+"F0.wireOp",EDGE,"E25.5"),sQuery(id+"F0.wireOp",EDGE,"E25.6"),sQuery(id+"F0.wireOp",EDGE,"E25.7")])],"isStart":false});
            extrude(context, id + "F17", {"entities" : qUnion([Q0, Q1, Q2]), "operationType" : NewBodyOperationType.ADD, "endBound" : BoundingType.UP_TO_SURFACE, "endBoundEntityFace" : qUnion([Q3]), "depth" : 25 * mm});
        }
    });
